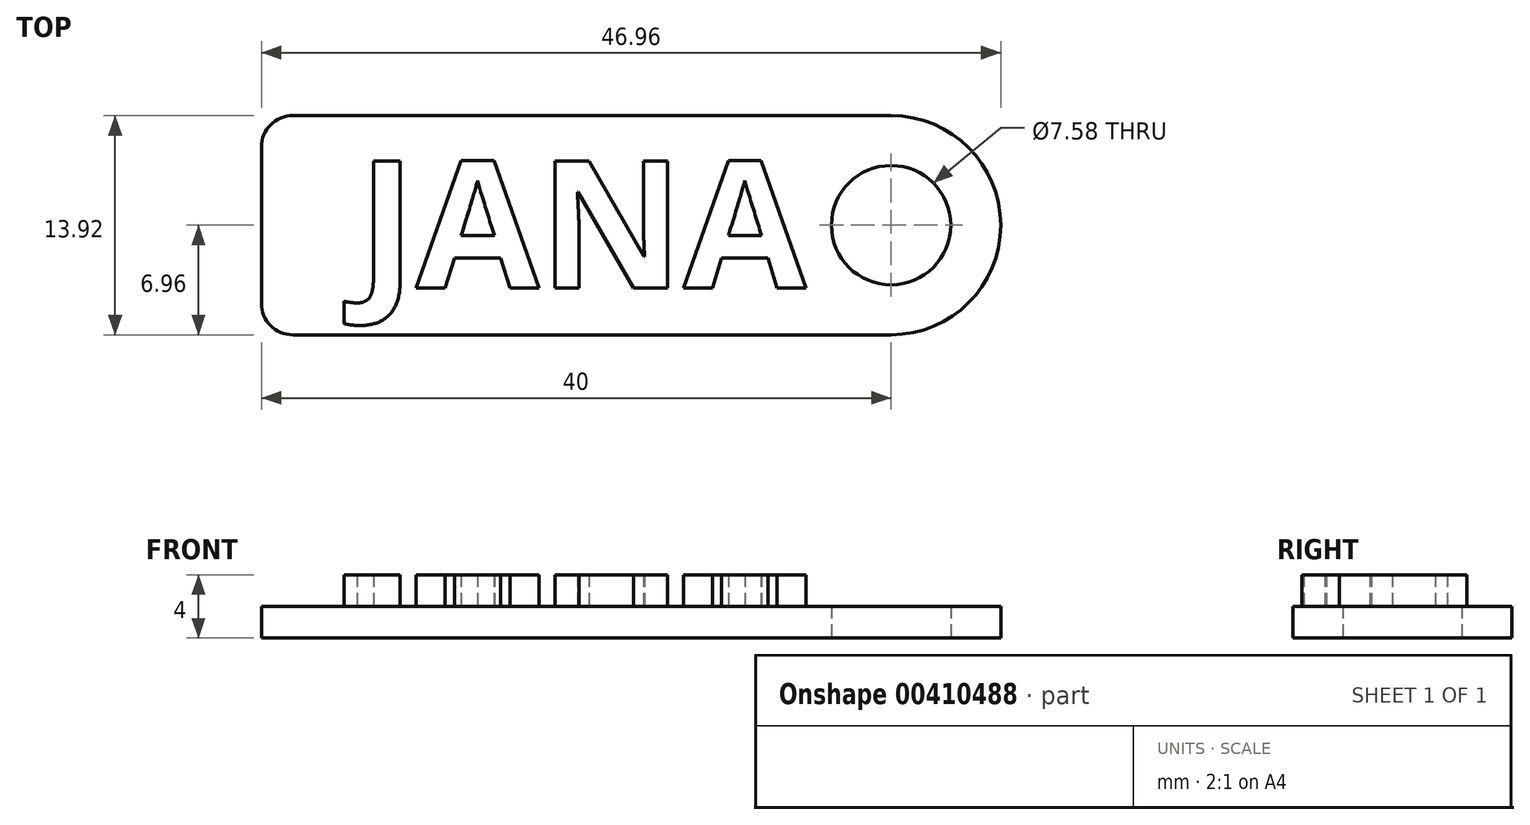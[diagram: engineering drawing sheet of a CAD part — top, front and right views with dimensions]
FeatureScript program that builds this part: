
annotation { "Feature Type Name" : "Feature", "Feature Type Description" : "" }
export const myFeature = defineFeature(function(context is Context, id is Id, definition is map)
    precondition{}
    {
        {
            var Q0;
            Q0=qCreatedBy(makeId("Top.planeOp"),FACE);
            var sketch = newSketch(context, id + "F0", { "sketchPlane" : qUnion([Q0])});
            skLineSegment(sketch, "E0.bottom", {"start": v(-20, 6.96) * mm, "end": v(20, 6.96) * mm});
            skLineSegment(sketch, "E0.top", {"start": v(-20, -6.96) * mm, "end": v(20, -6.96) * mm});
            skLineSegment(sketch, "E0.left", {"start": v(-20, 6.96) * mm, "end": v(-20, -6.96) * mm});
            skLineSegment(sketch, "E0.right", {"start": v(20, 6.96) * mm, "end": v(20, -6.96) * mm});
            skPoint(sketch, "E0.middle", {"position": v(0, 0) * mm});
            skPoint(sketch, "E1.startSnap0", {"position": v(20, 0) * mm});
            skArc(sketch, "E2", {"start": v(20, -6.96) * mm, "mid": v(26.96, 0) * mm, "end": v(20, 6.96) * mm});
            skCircle(sketch, "E3", {"center": v(20, 0) * mm, "radius": 3.8 * mm});
            skSolve(sketch);
        }
        {
            var Q0;
            {var subQ2=sQuery(id+"F0.wireOp",EDGE,"E0.bottom");Q0=makeQuery(id+"F0.imprint","IMPRINT",FACE,{"disambiguationData":[TD([[makeQuery(id+"F0.imprint","IMPRINT",EDGE,{"derivedFrom":subQ2}),-1.0]])]});}
            var Q1;
            {var subQ0=sQuery(id+"F0.wireOp",EDGE,"E2");Q1=makeQuery(id+"F0.imprint","IMPRINT",FACE,{"disambiguationData":[TD([[makeQuery(id+"F0.imprint","IMPRINT",EDGE,{"derivedFrom":subQ0}),1.0]])]});}
            extrude(context, id + "F1", {"entities" : qUnion([Q0, Q1]), "depth" : 2 * mm});
        }
        {
            var Q0;
            Q0=makeQuery(id+"F1.opExtrude","SWEPT_EDGE",EDGE,{"disambiguationData":[OSD([sQuery(id+"F0.wireOp",EDGE,"E0.bottom"),sQuery(id+"F0.wireOp",EDGE,"E0.left")])]});
            var Q1;
            Q1=makeQuery(id+"F1.opExtrude","SWEPT_EDGE",EDGE,{"disambiguationData":[OSD([sQuery(id+"F0.wireOp",EDGE,"E0.top"),sQuery(id+"F0.wireOp",EDGE,"E0.left")])]});
            fillet(context, id + "F2", {"entities" : qUnion([Q0, Q1]), "radius" : 2 * mm, "tangentPropagation" : true, "allowEdgeOverflow" : false});
        }
        {
            var Q0;
            Q0=makeQuery(id+"F1.opExtrude","CAP_FACE",FACE,{"disambiguationData":[OSD([sQuery(id+"F0.wireOp",EDGE,"E0.bottom"),sQuery(id+"F0.wireOp",EDGE,"E0.top"),sQuery(id+"F0.wireOp",EDGE,"E0.left"),sQuery(id+"F0.wireOp",EDGE,"E2"),sQuery(id+"F0.wireOp",EDGE,"E3")])],"isStart":false});
            var sketch = newSketch(context, id + "F3", { "sketchPlane" : qUnion([Q0])});
            skText(sketch, "E4", { "text": "JANA", "fontName": "OpenSans-Bold.ttf"});
            const initialGuessF3  = {"E4": [-0.0139, -0.004, 1, 0, 0.00813]};
            skSetInitialGuess(sketch, initialGuessF3);
            skSolve(sketch);
        }
        {
            var Q0;
            Q0=qSketchRegion(id+"F3",true);
            extrude(context, id + "F4", {"entities" : qUnion([Q0]), "operationType" : NewBodyOperationType.ADD, "depth" : 2 * mm});
        }
    });
